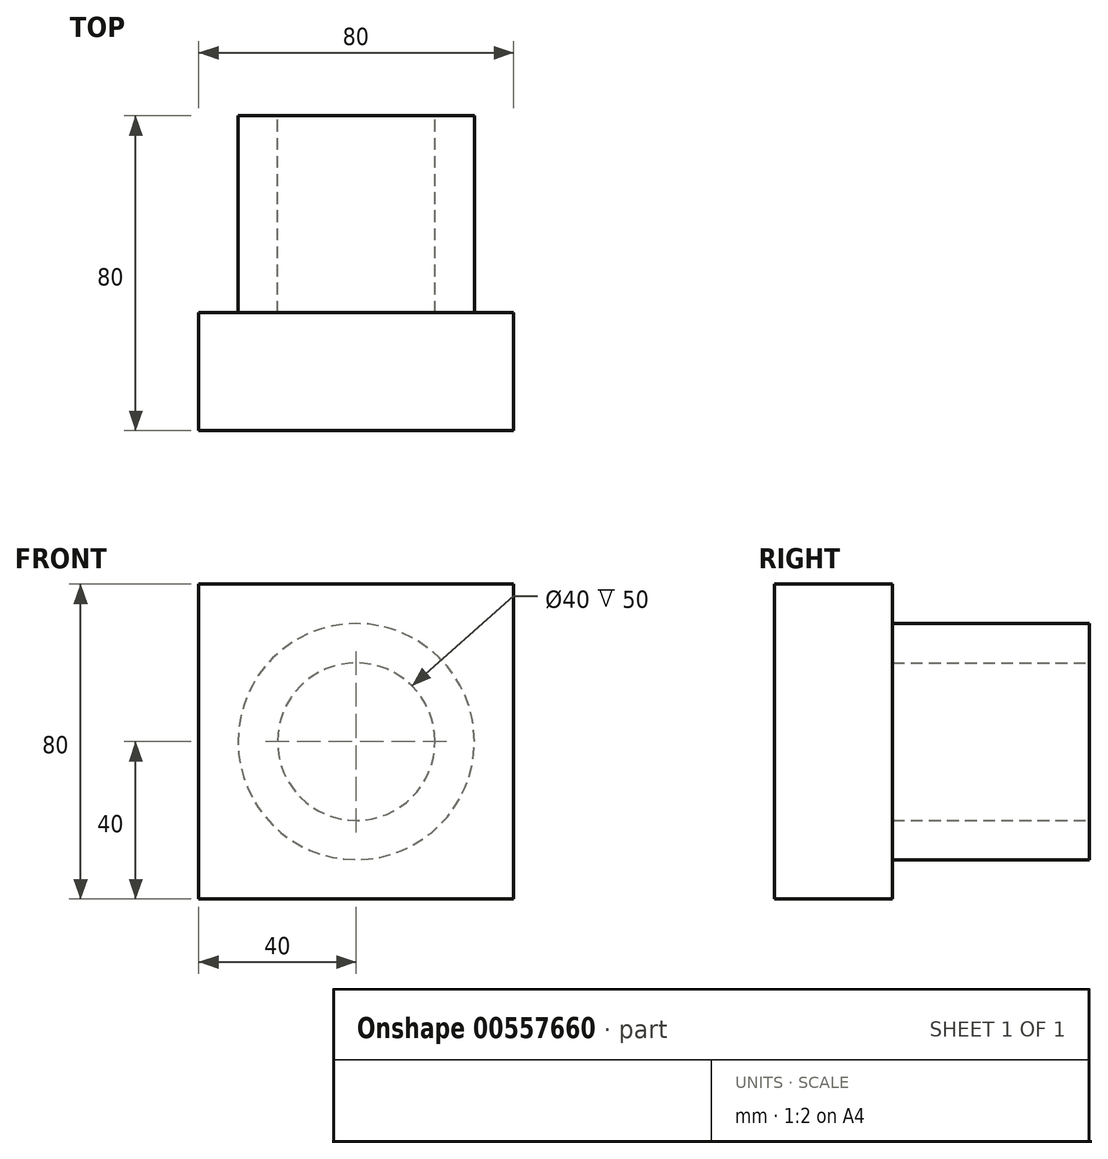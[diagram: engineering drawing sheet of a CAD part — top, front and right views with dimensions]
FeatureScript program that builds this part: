
annotation { "Feature Type Name" : "Feature", "Feature Type Description" : "" }
export const myFeature = defineFeature(function(context is Context, id is Id, definition is map)
    precondition{}
    {
        {
            var Q0;
            Q0=qCreatedBy(makeId("Front.planeOp"),FACE);
            var sketch = newSketch(context, id + "F0", { "sketchPlane" : qUnion([Q0])});
            skLineSegment(sketch, "E0.bottom", {"start": v(-40, 40) * mm, "end": v(40, 40) * mm});
            skLineSegment(sketch, "E0.top", {"start": v(-40, -40) * mm, "end": v(40, -40) * mm});
            skLineSegment(sketch, "E0.left", {"start": v(-40, 40) * mm, "end": v(-40, -40) * mm});
            skLineSegment(sketch, "E0.right", {"start": v(40, 40) * mm, "end": v(40, -40) * mm});
            skPoint(sketch, "E0.middle", {"position": v(0, 0) * mm});
            skSolve(sketch);
        }
        {
            var Q0;
            Q0 = qSketchRegion(id + "F0", true);
            var Q1;
            Q1=makeQuery(id+"F0.imprint","IMPRINT",FACE,{"disambiguationData":[TD([[makeQuery(id+"F0.imprint","IMPRINT",EDGE,{"derivedFrom":sQuery(id+"F0.wireOp",EDGE,"E0.bottom")}),-1.0]])]});
            extrude(context, id + "F1", {"entities" : qUnion([Q0, Q1]), "depth" : 30 * mm, "offsetDistance" : 25 * mm});
        }
        {
            var Q0;
            Q0=makeQuery(id+"F1.opExtrude","CAP_FACE",FACE,{"disambiguationData":[OSD([sQuery(id+"F0.wireOp",EDGE,"E0.bottom"),sQuery(id+"F0.wireOp",EDGE,"E0.top"),sQuery(id+"F0.wireOp",EDGE,"E0.left"),sQuery(id+"F0.wireOp",EDGE,"E0.right")])],"isStart":true});
            var sketch = newSketch(context, id + "F2", { "sketchPlane" : qUnion([Q0])});
            skCircle(sketch, "E1", {"center": v(0, 0) * mm, "radius": 30 * mm});
            skSolve(sketch);
        }
        {
            var Q0;
            Q0=makeQuery(id+"F2.imprint","IMPRINT",FACE,{"disambiguationData":[TD([[makeQuery(id+"F2.imprint","IMPRINT",EDGE,{"derivedFrom":sQuery(id+"F2.wireOp",EDGE,"E1")}),1.0]])]});
            extrude(context, id + "F3", {"entities" : qUnion([Q0]), "operationType" : NewBodyOperationType.ADD, "depth" : 50 * mm, "offsetDistance" : 25 * mm});
        }
        {
            var Q0;
            Q0=makeQuery(id+"F3.opExtrude","CAP_FACE",FACE,{"disambiguationData":[OSD([sQuery(id+"F2.wireOp",EDGE,"E1")])],"isStart":false});
            var sketch = newSketch(context, id + "F4", { "sketchPlane" : qUnion([Q0])});
            skCircle(sketch, "E2", {"center": v(0, 0) * mm, "radius": 20 * mm});
            skSolve(sketch);
        }
        {
            var Q0;
            Q0=makeQuery(id+"F4.imprint","IMPRINT",FACE,{"disambiguationData":[TD([[makeQuery(id+"F4.imprint","IMPRINT",EDGE,{"derivedFrom":sQuery(id+"F4.wireOp",EDGE,"E2")}),1.0]])]});
            extrude(context, id + "F5", {"entities" : qUnion([Q0]), "operationType" : NewBodyOperationType.REMOVE, "oppositeDirection" : true, "depth" : 50 * mm, "offsetDistance" : 25 * mm});
        }
    });
